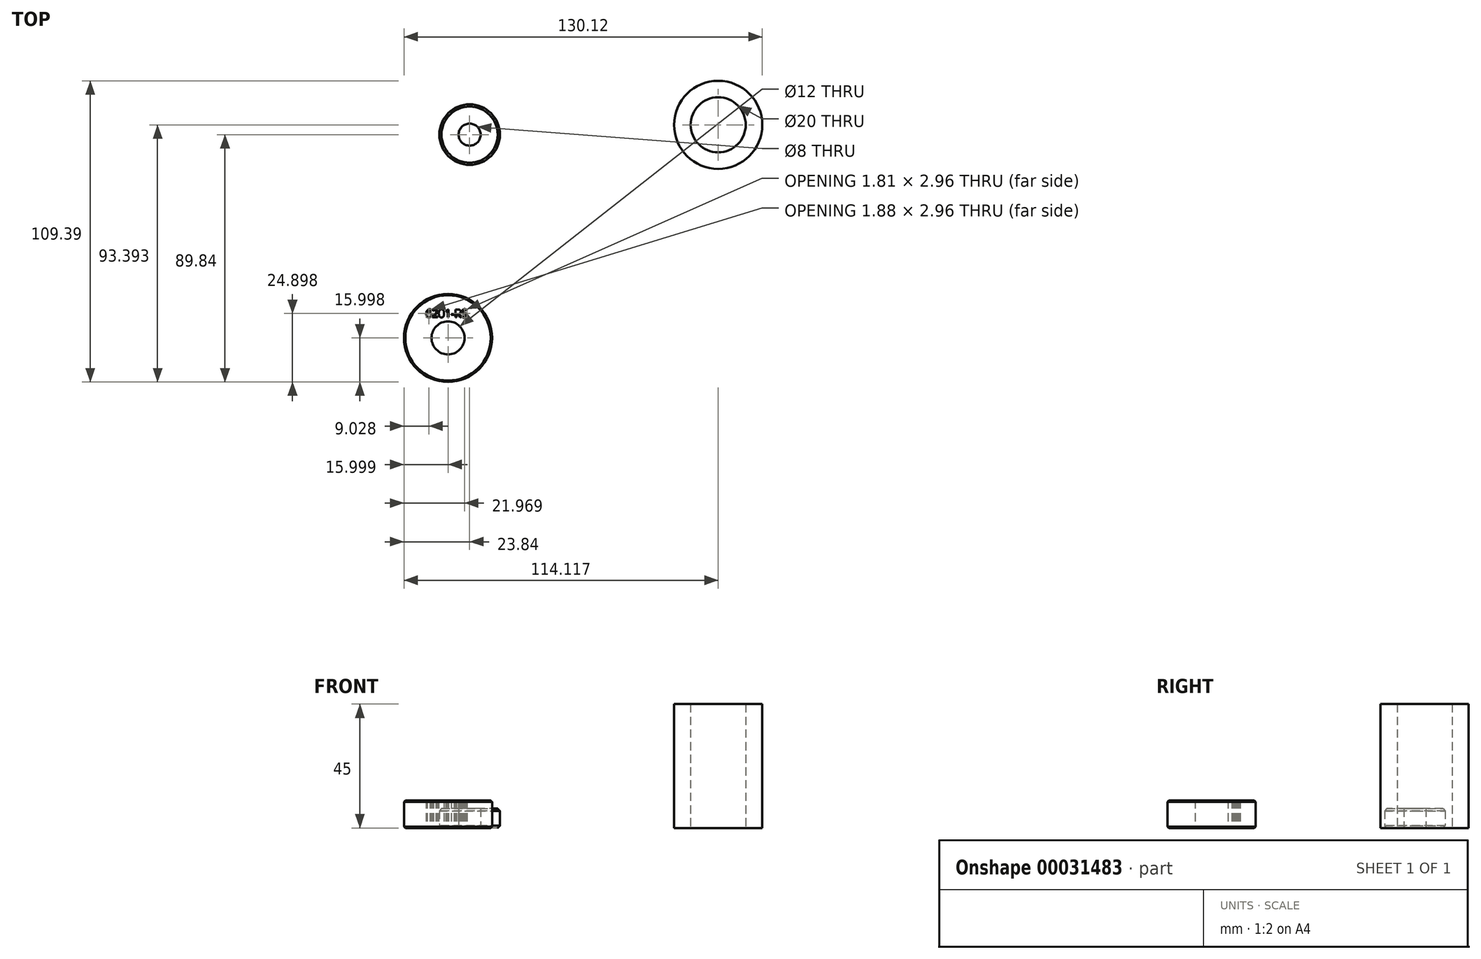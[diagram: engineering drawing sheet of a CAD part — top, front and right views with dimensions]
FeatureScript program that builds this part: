
annotation { "Feature Type Name" : "Feature", "Feature Type Description" : "" }
export const myFeature = defineFeature(function(context is Context, id is Id, definition is map)
    precondition{}
    {
        {
            var Q0;
            Q0=qCreatedBy(makeId("Top.planeOp"),FACE);
            var sketch = newSketch(context, id + "F0", { "sketchPlane" : qUnion([Q0]), "asVersion" : FeatureScriptVersionNumber.V236_DEFAULT_MAX_ASSEMBLIES});
            skCircle(sketch, "E0", {"center": v(-54.52, 42.58) * mm, "radius": 4 * mm});
            skCircle(sketch, "E1", {"center": v(-54.52, 42.58) * mm, "radius": 11 * mm});
            skSolve(sketch);
        }
        {
            var Q0;
            Q0=makeQuery(id+"F0.imprint","IMPRINT",FACE,{"disambiguationData":[TD([[makeQuery(id+"F0.imprint","IMPRINT",EDGE,{"derivedFrom":sQuery(id+"F0.wireOp",EDGE,"E0")}),-1.0]])]});
            extrude(context, id + "F1", {"entities" : qUnion([Q0]), "depth" : 7 * mm});
        }
        {
            var Q0;
            Q0=makeQuery(id+"F1.opExtrude","CAP_EDGE",EDGE,{"disambiguationData":[OSD([sQuery(id+"F0.wireOp",EDGE,"E1")])],"isStart":false});
            var Q1;
            Q1=makeQuery(id+"F1.opExtrude","CAP_EDGE",EDGE,{"disambiguationData":[OSD([sQuery(id+"F0.wireOp",EDGE,"E1")])],"isStart":true});
            chamfer(context, id + "F2", {"entities" : qUnion([Q0, Q1]), "width" : .8 * mm, "tangentPropagation" : true});
        }
        {
            var Q0;
            Q0=qCreatedBy(makeId("Top.planeOp"),FACE);
            var sketch = newSketch(context, id + "F3", { "sketchPlane" : qUnion([Q0]), "asVersion" : FeatureScriptVersionNumber.V236_DEFAULT_MAX_ASSEMBLIES});
            skCircle(sketch, "E2", {"center": v(35.76, 46.13) * mm, "radius": 10 * mm});
            skCircle(sketch, "E3", {"center": v(35.76, 46.13) * mm, "radius": 16 * mm});
            skSolve(sketch);
        }
        {
            var Q0;
            Q0=makeQuery(id+"F3.imprint","IMPRINT",FACE,{"disambiguationData":[TD([[makeQuery(id+"F3.imprint","IMPRINT",EDGE,{"derivedFrom":sQuery(id+"F3.wireOp",EDGE,"E2")}),-1.0]])]});
            extrude(context, id + "F4", {"entities" : qUnion([Q0]), "depth" : 45 * mm});
        }
        {
            var Q0;
            Q0=qCreatedBy(makeId("Top.planeOp"),FACE);
            var sketch = newSketch(context, id + "F5", { "sketchPlane" : qUnion([Q0])});
            skCircle(sketch, "E4", {"center": v(-62.36, -31.26) * mm, "radius": 6 * mm});
            skCircle(sketch, "E5", {"center": v(-62.36, -31.26) * mm, "radius": 16 * mm});
            skText(sketch, "E6", { "text": "6201-RS", "fontName": "OpenSans-Regular.ttf"});
            const initialGuessF5  = {"E6": [-0.0705, -0.0238, 1, 0, 0.0029]};
            skSetInitialGuess(sketch, initialGuessF5);
            skSolve(sketch);
        }
        {
            var Q0;
            Q0 = qSketchRegion(id + "F5", true);
            extrude(context, id + "F6", {"entities" : qUnion([Q0]), "depth" : 10 * mm});
        }
        {
            var Q0;
            Q0=makeQuery(id+"F6.opExtrude","CAP_EDGE",EDGE,{"disambiguationData":[OSD([sQuery(id+"F5.wireOp",EDGE,"E5")])],"isStart":false});
            var Q1;
            Q1=makeQuery(id+"F6.opExtrude","CAP_EDGE",EDGE,{"disambiguationData":[OSD([sQuery(id+"F5.wireOp",EDGE,"E5")])],"isStart":true});
            chamfer(context, id + "F7", {"entities" : qUnion([Q0, Q1]), "width" : .5 * mm, "tangentPropagation" : true});
        }
    });
